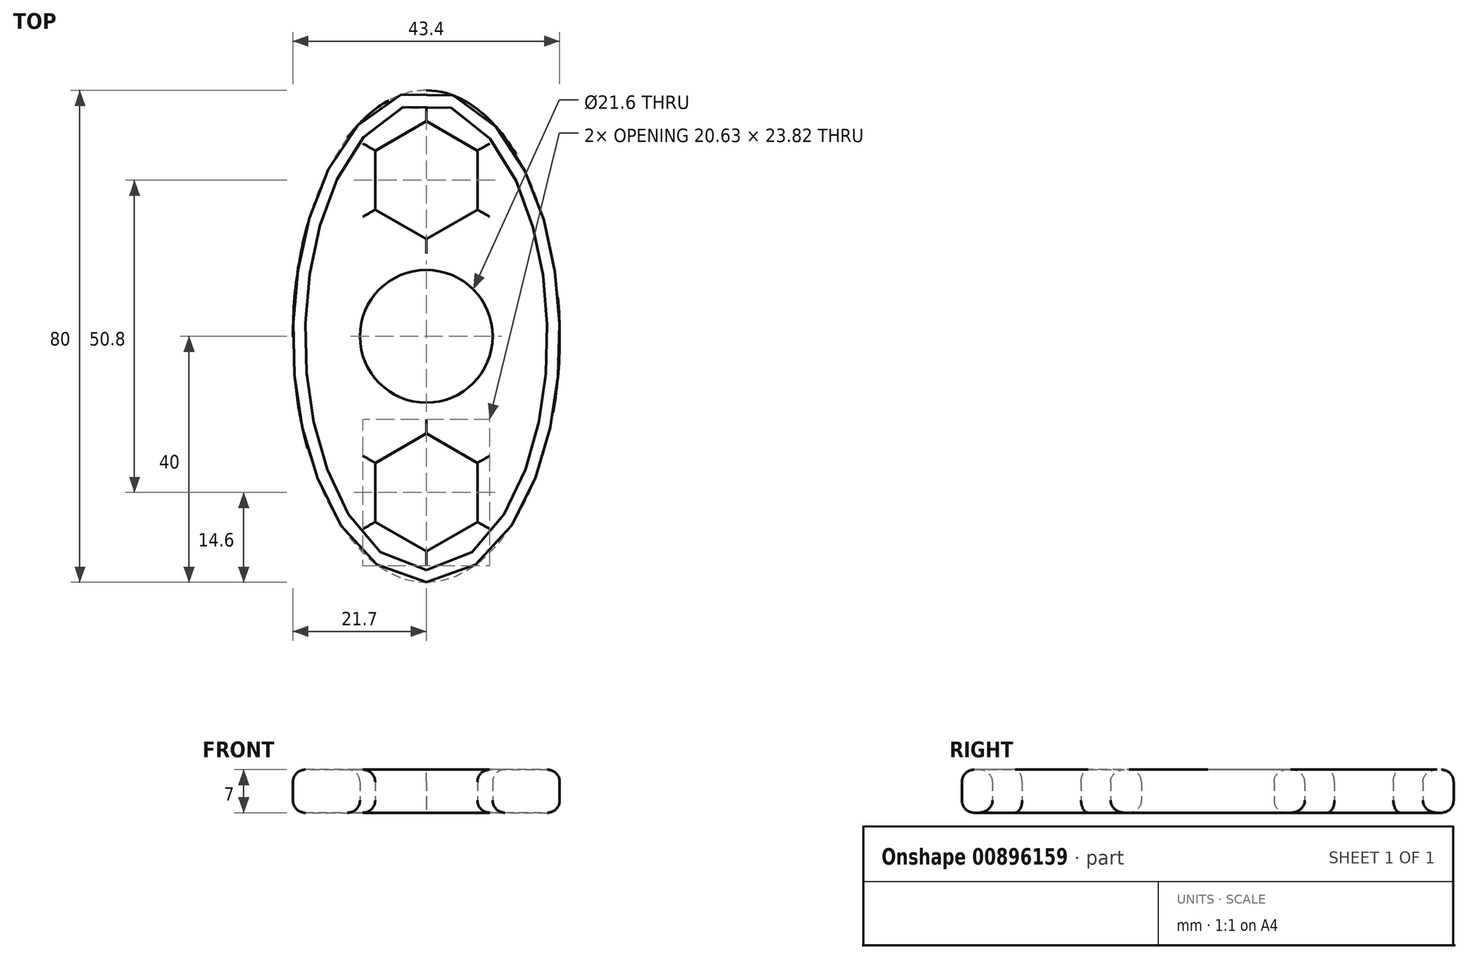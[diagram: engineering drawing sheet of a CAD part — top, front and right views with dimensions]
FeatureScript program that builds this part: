
annotation { "Feature Type Name" : "Feature", "Feature Type Description" : "" }
export const myFeature = defineFeature(function(context is Context, id is Id, definition is map)
    precondition{}
    {
        {
            var Q0;
            Q0=qCreatedBy(makeId("Top.planeOp"),FACE);
            var sketch = newSketch(context, id + "F0", { "sketchPlane" : qUnion([Q0])});
            skCircle(sketch, "E0", {"center": v(0, 0) * mm, "radius": 10.8 * mm});
            skLineSegment(sketch, "E1", {"start": v(0, 0) * mm, "end": v(0, 40) * mm, "construction": true});
            skLineSegment(sketch, "E2", {"start": v(0, 0) * mm, "end": v(0, -40) * mm, "construction": true});
            skCircle(sketch, "E3.cCircle", {"center": v(0, 25.4) * mm, "radius": 8.31 * mm, "construction": true});
            skLineSegment(sketch, "E3.0", {"start": v(8.31, 30.2) * mm, "end": v(8.31, 20.6) * mm});
            skLineSegment(sketch, "E3.1", {"start": v(8.31, 20.6) * mm, "end": v(0, 15.8) * mm});
            skLineSegment(sketch, "E3.2", {"start": v(0, 15.8) * mm, "end": v(-8.31, 20.6) * mm});
            skLineSegment(sketch, "E3.3", {"start": v(-8.31, 20.6) * mm, "end": v(-8.31, 30.2) * mm});
            skLineSegment(sketch, "E3.4", {"start": v(-8.31, 30.2) * mm, "end": v(0, 35) * mm});
            skLineSegment(sketch, "E3.5", {"start": v(0, 35) * mm, "end": v(8.31, 30.2) * mm});
            skPoint(sketch, "E3.0.midPoint", {"position": v(8.31, 25.4) * mm});
            skCircle(sketch, "E4.cCircle", {"center": v(0, -25.4) * mm, "radius": 8.31 * mm, "construction": true});
            skLineSegment(sketch, "E4.0", {"start": v(8.31, -20.6) * mm, "end": v(8.31, -30.2) * mm});
            skLineSegment(sketch, "E4.1", {"start": v(8.31, -30.2) * mm, "end": v(0, -35) * mm});
            skLineSegment(sketch, "E4.2", {"start": v(0, -35) * mm, "end": v(-8.31, -30.2) * mm});
            skLineSegment(sketch, "E4.3", {"start": v(-8.31, -30.2) * mm, "end": v(-8.31, -20.6) * mm});
            skLineSegment(sketch, "E4.4", {"start": v(-8.31, -20.6) * mm, "end": v(0, -15.8) * mm});
            skLineSegment(sketch, "E4.5", {"start": v(0, -15.8) * mm, "end": v(8.31, -20.6) * mm});
            skPoint(sketch, "E4.0.midPoint", {"position": v(8.31, -25.4) * mm});
            skEllipse(sketch, "E5", {"center": v(0, 0) * mm, "majorRadius": 40 * mm, "minorRadius": 21.7 * mm, "majorAxis": v(0, -1)});
            skSolve(sketch);
        }
        {
            var Q0;
            Q0 = qSketchRegion(id + "F0", true);
            extrude(context, id + "F1", {"entities" : qUnion([Q0]), "depth" : 7 * mm, "offsetDistance" : 25 * mm});
        }
        {
            var Q0;
            Q0=makeQuery(id+"F1.opExtrude","CAP_FACE",FACE,{"disambiguationData":[OSD([sQuery(id+"F0.wireOp",EDGE,"E0"),sQuery(id+"F0.wireOp",EDGE,"E3.0"),sQuery(id+"F0.wireOp",EDGE,"E3.1"),sQuery(id+"F0.wireOp",EDGE,"E3.2"),sQuery(id+"F0.wireOp",EDGE,"E3.3"),sQuery(id+"F0.wireOp",EDGE,"E3.4"),sQuery(id+"F0.wireOp",EDGE,"E3.5"),sQuery(id+"F0.wireOp",EDGE,"E4.0"),sQuery(id+"F0.wireOp",EDGE,"E4.1"),sQuery(id+"F0.wireOp",EDGE,"E4.2"),sQuery(id+"F0.wireOp",EDGE,"E4.3"),sQuery(id+"F0.wireOp",EDGE,"E4.4"),sQuery(id+"F0.wireOp",EDGE,"E4.5"),sQuery(id+"F0.wireOp",EDGE,"E5")])],"isStart":false});
            fillet(context, id + "F2", {"entities" : qUnion([Q0]), "radius" : 2 * mm, "tangentPropagation" : true, "allowEdgeOverflow" : false});
        }
        {
            var Q0;
            Q0=makeQuery(id+"F1.opExtrude","CAP_FACE",FACE,{"disambiguationData":[OSD([sQuery(id+"F0.wireOp",EDGE,"E0"),sQuery(id+"F0.wireOp",EDGE,"E3.0"),sQuery(id+"F0.wireOp",EDGE,"E3.1"),sQuery(id+"F0.wireOp",EDGE,"E3.2"),sQuery(id+"F0.wireOp",EDGE,"E3.3"),sQuery(id+"F0.wireOp",EDGE,"E3.4"),sQuery(id+"F0.wireOp",EDGE,"E3.5"),sQuery(id+"F0.wireOp",EDGE,"E4.0"),sQuery(id+"F0.wireOp",EDGE,"E4.1"),sQuery(id+"F0.wireOp",EDGE,"E4.2"),sQuery(id+"F0.wireOp",EDGE,"E4.3"),sQuery(id+"F0.wireOp",EDGE,"E4.4"),sQuery(id+"F0.wireOp",EDGE,"E4.5"),sQuery(id+"F0.wireOp",EDGE,"E5")])],"isStart":true});
            fillet(context, id + "F3", {"entities" : qUnion([Q0]), "radius" : 2 * mm, "tangentPropagation" : true, "allowEdgeOverflow" : false});
        }
    });
